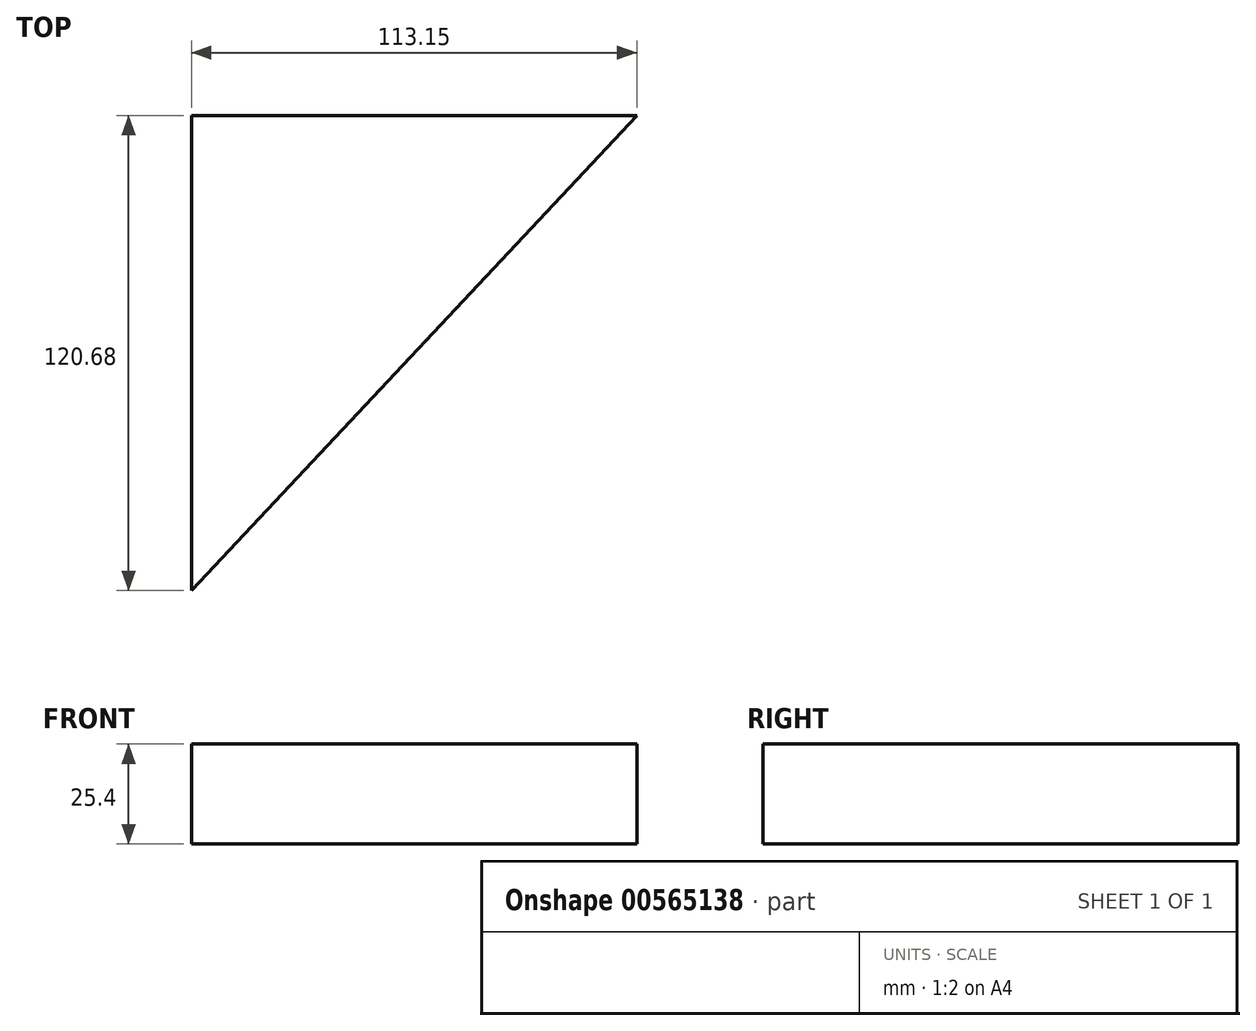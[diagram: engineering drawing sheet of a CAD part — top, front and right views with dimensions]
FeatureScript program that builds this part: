
annotation { "Feature Type Name" : "Feature", "Feature Type Description" : "" }
export const myFeature = defineFeature(function(context is Context, id is Id, definition is map)
    precondition{}
    {
        {
            var Q0;
            Q0=qCreatedBy(makeId("Top.planeOp"),FACE);
            var sketch = newSketch(context, id + "F0", { "sketchPlane" : qUnion([Q0])});
            skLineSegment(sketch, "E0.bottom", {"start": v(113.15, -60.34) * mm, "end": v(-113.15, -60.34) * mm});
            skLineSegment(sketch, "E0.top", {"start": v(113.15, 60.34) * mm, "end": v(-113.15, 60.34) * mm});
            skLineSegment(sketch, "E0.left", {"start": v(113.15, -60.34) * mm, "end": v(113.15, 60.34) * mm});
            skLineSegment(sketch, "E0.right", {"start": v(-113.15, -60.34) * mm, "end": v(-113.15, 60.34) * mm});
            skPoint(sketch, "E0.middle", {"position": v(0, 0) * mm});
            skLineSegment(sketch, "E1", {"start": v(-113.15, -60.34) * mm, "end": v(0, 60.34) * mm});
            skSolve(sketch);
        }
        {
            var Q0;
            {var subQ0=sQuery(id+"F0.wireOp",EDGE,"E0.right");Q0=makeQuery(id+"F0.imprint","IMPRINT",FACE,{"disambiguationData":[TD([[makeQuery(id+"F0.imprint","IMPRINT",EDGE,{"derivedFrom":subQ0}),-1.0]])]});}
            extrude(context, id + "F1", {"entities" : qUnion([Q0]), "depth" : 25.4 * mm, "offsetDistance" : 25.4 * mm});
        }
    });
